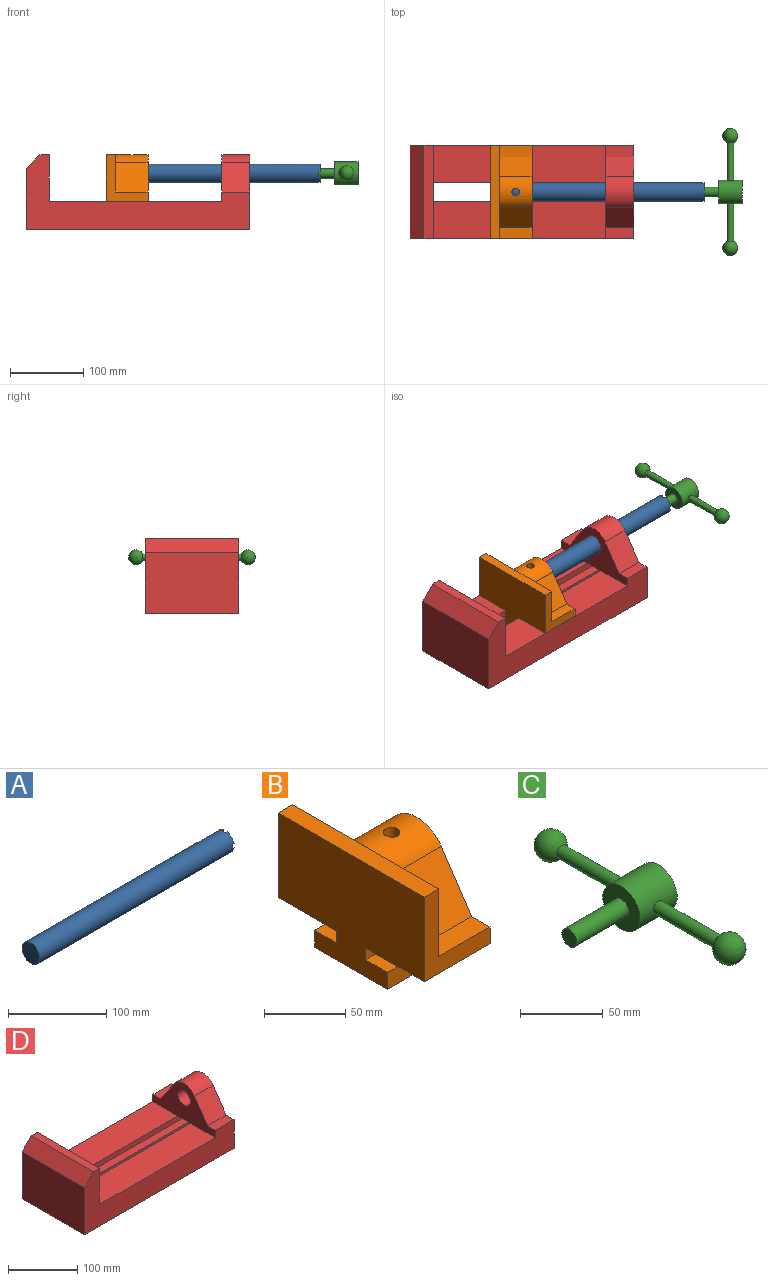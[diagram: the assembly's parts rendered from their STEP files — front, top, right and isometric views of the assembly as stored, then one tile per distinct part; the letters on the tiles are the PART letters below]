
ASSEMBLY  parts=4 mates=3
PART A: 20 faces, bbox 279.4x25.4x25.4 mm
  f0: cylinder r=12.7mm len=279.4mm, axis (1,0,0), area 22243.2mm2, adj f1,f2,f3,f4,f5,f8,f9,f10
  f1: plane 9.9x9.9mm, normal (1,0,0), area 62.3mm2, adj f0,f6,f12,f17
  f2: plane 9.9x9.9mm, normal (1,0,0), area 62.3mm2, adj f0,f6,f9,f14
  f3: plane 9.9x9.9mm, normal (1,0,0), area 62.3mm2, adj f0,f6,f15,f18
  f4: plane 25.4x25.4mm, normal (-1,0,0), area 506.7mm2, adj f0
  f5: plane 9.9x9.9mm, normal (1,0,0), area 62.3mm2, adj f0,f6,f8,f13
  f6: cylinder r=6.35mm len=25.4mm, axis (1,0,0), area 960.3mm2, adj f1,f2,f3,f5,f7,f8,f9,f10
  f7: plane 12.7x12.7mm, normal (1,0,0), area 126.7mm2, adj f6
  f8: plane 6.62x2.54mm, normal (0,0,1), area 16.8mm2, adj f0,f5,f6,f10
  f9: plane 6.62x2.54mm, normal (0,0,-1), area 16.8mm2, adj f0,f2,f6,f10
  f10: plane 6.88x5.08mm, normal (1,0,0), area 32.7mm2, adj f0,f6,f8,f9
  f11: plane 6.88x5.08mm, normal (1,0,0), area 32.7mm2, adj f0,f6,f12,f13
  f12: plane 6.62x2.54mm, normal (0,1,0), area 16.8mm2, adj f0,f1,f6,f11
  f13: plane 6.62x2.54mm, normal (0,-1,0), area 16.8mm2, adj f0,f5,f6,f11
  f14: plane 6.62x2.54mm, normal (0,-1,0), area 16.8mm2, adj f0,f2,f6,f16
  f15: plane 6.62x2.54mm, normal (0,1,0), area 16.8mm2, adj f0,f3,f6,f16
  f16: plane 6.88x5.08mm, normal (1,0,0), area 32.7mm2, adj f0,f6,f14,f15
  f17: plane 6.62x2.54mm, normal (0,0,1), area 16.8mm2, adj f0,f1,f6,f19
  f18: plane 6.62x2.54mm, normal (0,0,-1), area 16.8mm2, adj f0,f3,f6,f19
  f19: plane 6.88x5.08mm, normal (1,0,0), area 32.7mm2, adj f0,f6,f17,f18
PART B: 24 faces, bbox 57.2x127x85.1 mm
  f0: plane 127x85.09mm, normal (1,0,0), area 5190mm2, adj f1,f2,f3,f4,f5,f6,f8,f9
  f1: plane 63.5x57.15mm, normal (0,0,-1), area 3629mm2, adj f0,f2,f12,f13
  f2: plane 57.15x12.7mm, normal (0,1,0), area 725.8mm2, adj f0,f1,f3,f13
  f3: plane 57.15x19.05mm, normal (0,0,1), area 1088.7mm2, adj f0,f2,f4,f13
  f4: plane 57.15x8.89mm, normal (0,1,0), area 508.1mm2, adj f0,f3,f5,f13
  f5: plane 57.15x50.8mm, normal (0,0,-1), area 2903.2mm2, adj f0,f4,f6,f13
  f6: plane 63.5x57.15mm, normal (0,1,0), area 1371mm2, adj f0,f5,f7,f13,f14,f17
  f7: plane 127x12.7mm, normal (0,0,1), area 1612.9mm2, adj f6,f8,f13,f17,f20
  f8: plane 63.5x57.15mm, normal (0,-1,0), area 1371mm2, adj f0,f7,f9,f13,f18,f20
  f9: plane 57.15x50.8mm, normal (0,0,-1), area 2903.2mm2, adj f0,f8,f10,f13
  f10: plane 57.15x8.89mm, normal (0,-1,0), area 508.1mm2, adj f0,f9,f11,f13
  f11: plane 57.15x19.05mm, normal (0,0,1), area 1088.7mm2, adj f0,f10,f12,f13
  f12: plane 57.15x12.7mm, normal (0,-1,0), area 725.8mm2, adj f0,f1,f11,f13
  f13: plane 127x85.09mm, normal (-1,0,0), area 9096.8mm2, adj f1,f2,f3,f4,f5,f6,f7,f8
  f14: plane 44.45x15.88mm, normal (0,0,1), area 705.6mm2, adj f0,f6,f16,f17
  f15: cylinder r=25.4mm len=44.45mm, axis (1,0,0), area 2131.3mm2, adj f0,f16,f17,f19,f20,f23
  f16: plane 44.45x39.55mm, normal (0,0.83,0.56), area 2116.9mm2, adj f0,f14,f15,f17
  f17: plane 63.5x50.8mm, normal (1,0,0), area 1700mm2, adj f6,f7,f14,f15,f16
  f18: plane 44.45x15.88mm, normal (0,0,1), area 705.6mm2, adj f0,f8,f19,f20
  f19: plane 44.45x39.55mm, normal (0,-0.83,0.56), area 2116.9mm2, adj f0,f15,f18,f20
  f20: plane 63.5x50.8mm, normal (1,0,0), area 1700mm2, adj f7,f8,f15,f18,f19
  f21: cylinder r=12.7mm len=44.45mm, axis (1,0,0), area 3464.2mm2, adj f0,f22,f23
  f22: plane 25.4x25.4mm, normal (1,0,0), area 506.7mm2, adj f21
  f23: cylinder r=5.08mm len=13.76mm, axis (0,0,1), area 414mm2, adj f15,f21
PART C: 9 faces, bbox 76.2x172.7x31.8 mm
  f0: cylinder r=15.88mm len=31.75mm, axis (-1,0,0), area 3041.6mm2, adj f1,f2,f5,f6
  f1: plane 31.75x31.75mm, normal (1,0,0), area 791.7mm2, adj f0
  f2: plane 31.75x31.75mm, normal (-1,0,0), area 665.1mm2, adj f0,f3
  f3: cylinder r=6.35mm len=44.45mm, axis (1,0,0), area 1773.5mm2, adj f2,f4
  f4: plane 12.7x12.7mm, normal (-1,0,0), area 126.7mm2, adj f3
  f5: cylinder r=4.45mm len=51.82mm, axis (0,1,0), area 1438.5mm2, adj f0,f8
  f6: cylinder r=4.45mm len=51.82mm, axis (0,-1,0), area 1438.5mm2, adj f0,f7
  f7: sphere r=10.16mm, area 1231.8mm2, adj f6
  f8: sphere r=10.16mm, area 1231.8mm2, adj f5
PART D: 28 faces, bbox 304.8x127x101.6 mm
  f0: plane 127x101.6mm, normal (1,0,0), area 7544.8mm2, adj f1,f8,f9,f11,f12,f13,f14,f15
  f1: plane 304.8x127mm, normal (0,0,-1), area 31774.1mm2, adj f0,f4,f7,f8,f9,f17,f27
  f2: plane 234.95x50.8mm, normal (0,0,1), area 11935.5mm2, adj f5,f7,f8,f21
  f3: plane 127x12.7mm, normal (0,0,1), area 1612.9mm2, adj f7,f8,f9,f10
  f4: plane 127x82.55mm, normal (-1,0,0), area 10483.8mm2, adj f1,f8,f9,f10
  f5: plane 127x63.5mm, normal (-1,0,0), area 4157.7mm2, adj f2,f6,f8,f9,f11,f12,f13,f14
  f6: plane 234.95x50.8mm, normal (0,0,1), area 11935.5mm2, adj f5,f7,f9,f23
  f7: plane 127x101.6mm, normal (1,0,0), area 9516.1mm2, adj f1,f2,f3,f6,f8,f9,f17,f18
  f8: plane 304.8x101.6mm, normal (0,1,0), area 13931.4mm2, adj f0,f1,f2,f3,f4,f5,f7,f10
  f9: plane 304.8x101.6mm, normal (0,-1,0), area 13931.4mm2, adj f0,f1,f3,f4,f5,f6,f7,f10
  f10: plane 127x19.05mm, normal (-0.71,0,0.71), area 3421.5mm2, adj f3,f4,f8,f9
  f11: plane 38.1x15.88mm, normal (0,0,1), area 604.8mm2, adj f0,f5,f8,f13
  f12: cylinder r=25.4mm len=42.19mm, axis (1,0,0), area 1896.6mm2, adj f0,f5,f13,f15
  f13: plane 39.55x38.1mm, normal (0,0.83,0.56), area 1814.5mm2, adj f0,f5,f11,f12
  f14: plane 38.1x15.88mm, normal (0,0,1), area 604.8mm2, adj f0,f5,f9,f15
  f15: plane 39.55x38.1mm, normal (0,-0.83,0.56), area 1814.5mm2, adj f0,f5,f12,f14
  f16: cylinder r=12.7mm len=38.1mm, axis (1,0,0), area 3040.2mm2, adj f0,f5
  f17: plane 273.05x16.51mm, normal (0,-1,0), area 4508.1mm2, adj f0,f1,f7,f18
  f18: plane 273.05x19.05mm, normal (0,0,1), area 5201.6mm2, adj f0,f7,f17,f19
  f19: plane 273.05x12.7mm, normal (0,-1,0), area 3467.7mm2, adj f0,f7,f18,f20
  f20: plane 273.05x19.05mm, normal (0,0,-1), area 5201.6mm2, adj f0,f7,f19,f21
  f21: plane 273.05x8.89mm, normal (0,-1,0), area 2427.4mm2, adj f0,f2,f7,f20,f22
  f22: plane 38.1x25.4mm, normal (0,0,-1), area 967.7mm2, adj f0,f5,f21,f23
  f23: plane 273.05x8.89mm, normal (0,1,0), area 2427.4mm2, adj f0,f6,f7,f22,f24
  f24: plane 273.05x19.05mm, normal (0,0,-1), area 5201.6mm2, adj f0,f7,f23,f25
  f25: plane 273.05x12.7mm, normal (0,1,0), area 3467.7mm2, adj f0,f7,f24,f26
  f26: plane 273.05x19.05mm, normal (0,0,1), area 5201.6mm2, adj f0,f7,f25,f27
  f27: plane 273.05x16.51mm, normal (0,1,0), area 4508.1mm2, adj f0,f1,f7,f26
PLACE A t=(382.19,116.19,84.03)mm
PLACE B t=(147.24,84.44,24.34)mm
PLACE C t=(417.11,116.19,84.03)mm
PLACE D t=(-18.85,52.69,7.83)mm fixed
MATE fastened B.f15 <-> A.f0  axis (1,0,0) through (102.79,116.19,84.03)mm
MATE slider A.f0 <-> D.f12  axis (1,0,0) through (242.49,116.19,84.03)mm
MATE fastened C.f0 <-> A.f0  axis (1,0,0) through (356.79,116.19,84.03)mm
